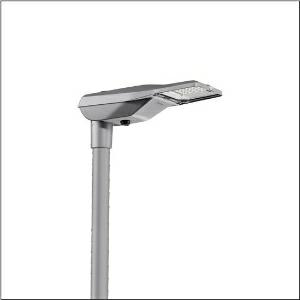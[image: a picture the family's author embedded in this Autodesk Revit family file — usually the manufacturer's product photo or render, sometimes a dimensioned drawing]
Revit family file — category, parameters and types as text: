
# Revit family: streetlight_sl_21_iq_micro___p0_5a_5xe1v31u08db_ec29
name_source: partatom
category: Lighting Fixtures
units: mm (PartAtom-declared; Revit-internal decimal feet)

## family parameters
Cut with Voids When Loaded = No
Host = Face
Light Source = No
Part Type = Normal
Room Calculation Point = No
Round Connector Dimension = Use Diameter
Shared = No

## types (1)
- --- (1 x LED, 5030 lm, 39.1 W, 3000K)
    Apparent Load = 39 VA
    CIE Flux Codes = 37 73 96 100 100
    Color Rendering = 70
    Color Temperature = 3000K
    Default Elevation = 1800 mm
    Description = Streetlight SL 21 iQ micro, mast luminaire, primary light control with lens, of PMMA, primary optical cover: cover, of toughened safety glass, transparent, light distribution: P0.5a, light emission: direct distribution, primary light characteristic: asymmetric, installation type: post-top, side-entry, LED, High Power LED, rated luminous flux: 5.030lm, luminous efficacy: 129lm/W, light colour: 730, colour temperature: 3000K, control gear: iQ-Street Remote, D4i with power reduction, control: pre-setting: logarithmic dimming characteristic, Street-Remote, Auto-Match, Temp-Guard, Lumen-Switch, Night-Set, Smart-Wire, Light-Fading, Desk-Remote (wireless, voltage-free reading and setting of iQ features in the workshop via application-optimized NFC function/RFID function), optimised constant luminous flux control (CLO 2.0), mains connection: 220..240V, AC, 50/60Hz, start of lifetime: 39W, end of service life: 41W, reduction: 17W, luminaire housing, of diecast aluminium, powder-coated, Siteco® metallic grey (DB 702S), corrosivity category C5 mid according to DIN EN ISO 12944, please order mast flange separately, inclination adjustable: 0°, 5°, 10°, 15°, sealing non-destructively replaceable, multi-level sealing system, length: 528mm, width: 235mm, height: 110mm, mast flange for spigot size: 42mm (side-entry): 5XC10008XM4, 60/48mm (side-entry/post-top): 5XC10108XM2, 76/60mm (side-entry/post-top): 5XC10108XM1, mounting height: 4..8m, Smart Interface below, protection rating (complete): IP66, insulation class (complete): insulation class II (safety insulation), certification: CE, ENEC, ENEC+, VDE, impact resistance: IK10, permissible operating ambient temperature for outdoor applications: -40..+50°C, standard-compliant lighting for roads and squares, packaging unit: 1 piece

Light Distribution: P0.5a
    Height = 110 mm
    Lamp = 1 x LED
    Lamp Light Flux = 5030 lm
    Lamp Power = 39.1 W
    Lamp count = 1
    Length = 528 mm
    Luminous efficacy = 129 lm/W
    Manufacturer = Siteco
    ModVariant = No
    Model = 5XE1V31U08DB
    Number of Poles = 1
    OnlyDefault = Yes
    Power Factor = 1
    Product Name = Streetlight SL 21 iQ micro | P0.5a
    Product group = mast luminaire | pylon top
    ProductGroupID = 6100
    Protection Class = Protection class II
    Protection Degree = IP 66
    RLX_Detail_Level = 1
    RLX_Emergency_Light_Flux = 0 lm
    RLX_Emergency_Type = 0
    RLX_Emergency_Type_DB = No
    RlxData = <blob elided: 98345 chars, md5=47d44ba0>
    Socket = socket
    Standby Power = 0 W
    System Light Flux = 5030 lm
    System Power = 39 W
    Type Comments = factory setting: luminous flux: 100 % | dim-lin: 254 | 765 mA
    Type Image = l_1277290.jpg
    URL = http://relux.com
    VarID = @adj_092389
    Voltage = 0 V
    Weight = 0.00 kg
    Width = 235 mm

## geometry (parser evidence)
native form markers: Blend x4, Sweep x12
no freeform markers — native parametric forms only
